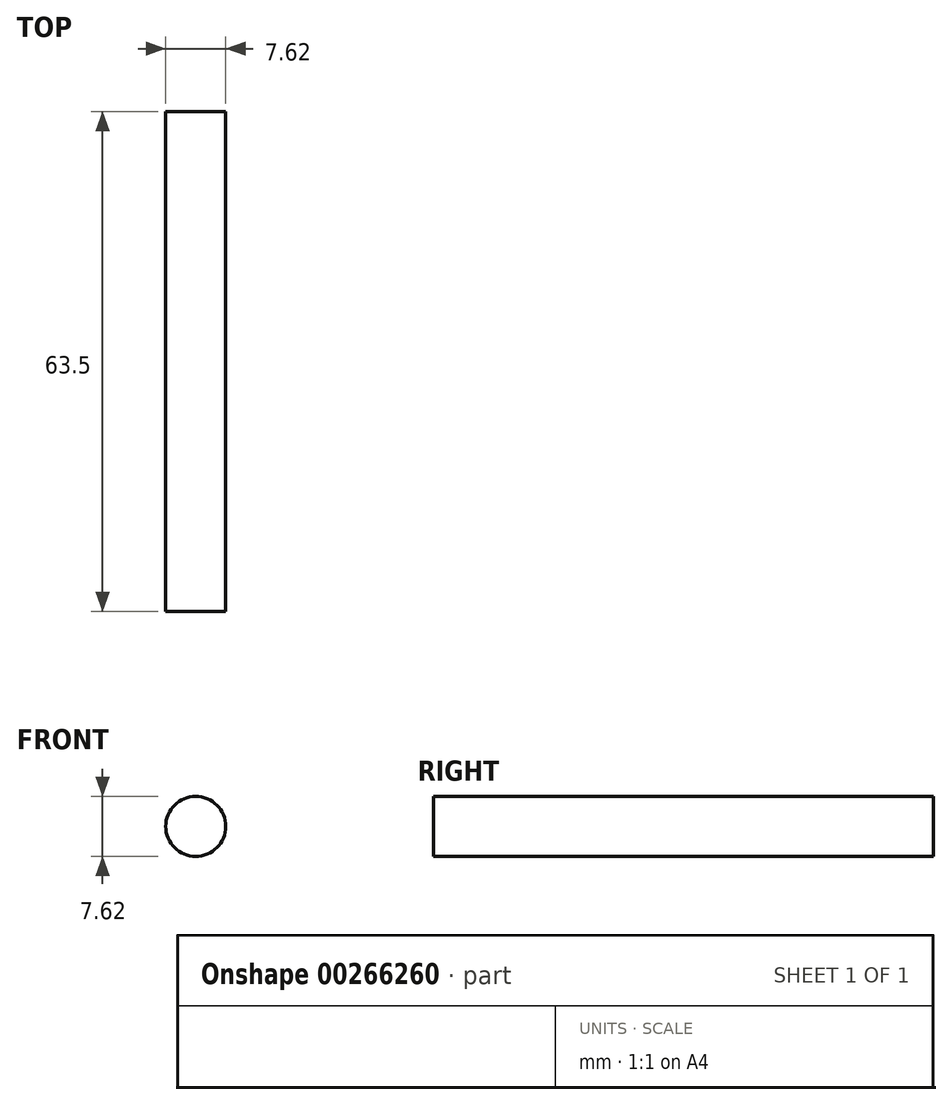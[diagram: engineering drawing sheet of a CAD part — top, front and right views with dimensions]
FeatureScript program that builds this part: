
annotation { "Feature Type Name" : "Feature", "Feature Type Description" : "" }
export const myFeature = defineFeature(function(context is Context, id is Id, definition is map)
    precondition{}
    {
        {
            var Q0;
            Q0=qCreatedBy(makeId("Front.planeOp"),FACE);
            var sketch = newSketch(context, id + "F0", { "sketchPlane" : qUnion([Q0])});
            skCircle(sketch, "E0", {"center": v(0, 0) * mm, "radius": 3.8 * mm});
            skSolve(sketch);
        }
        {
            var Q0;
            Q0=qSketchRegion(id+"F0",true);
            extrude(context, id + "F1", {"entities" : qUnion([Q0]), "depth" : 63.5 * mm});
        }
    });
